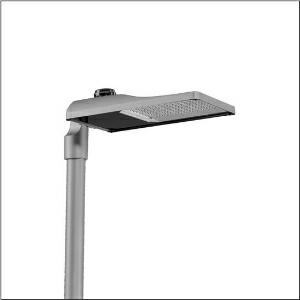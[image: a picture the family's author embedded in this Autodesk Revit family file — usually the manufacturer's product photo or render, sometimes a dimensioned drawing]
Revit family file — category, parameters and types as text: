
# Revit family: streetlight_sl_31_maxi___pl52_5xh8h75n08sa_385d
name_source: partatom
category: Lighting Fixtures
units: mm (PartAtom-declared; Revit-internal decimal feet)

## family parameters
Cut with Voids When Loaded = No
Host = Face
Light Source = No
Part Type = Normal
Room Calculation Point = No
Round Connector Dimension = Use Diameter
Shared = No

## types (1)
- --- (1 x LED, 22010 lm, 208.6 W, 2200K)
    Apparent Load = 209 VA
    CIE Flux Codes = 27 59 98 100 100
    Color Rendering = 70
    Color Temperature = 2200K
    Default Elevation = 1800 mm
    Description = Streetlight SL 31 maxi NEMA (7pin), Desk-Remote mast luminaire for post-top, side-entry; light control with lens of PMMA; light distribution: PL52, direct asymmetric distribution, for standard-compliant lighting for roads and squares; LED: luminous flux: 22.010lm, light colour: 722, colour temperature: 2200K; luminous efficacy: 105,5lm/W; control: pre-setting: linear dimming characteristic, flexible luminous flux parameterisation, time-dependent luminous flux control, constant luminous flux control, intelligent temperature release in ECG and LED module, overheat protection; luminaire housing, of diecast aluminium, Siteco® metallic grey (DB 702S), corrosivity category C5 high according to DIN EN ISO 12944; cover of toughened safety glass, transparent, opened without tools; mast flange of diecast aluminium, Siteco® metallic grey (DB 702S), spigot size: 76/60mm, mast flange included unmounted; with cable H07RN-F 3x 1.5mm², cable length: 14,5m, connection cable pre-assembled; mains connection: 220..240V, AC, 50/60Hz; power consumption (at start of service life): 208,6W / (at end of service life): 233,1W / (with reduced operation 50%): 88W; protection rating (complete): IP66; insulation class (complete): insulation class I (protective earthing); impact resistance: IK10; certification: CE, ENEC, ENEC+, VDE, UKCA; permissible operating ambient temperature for outdoor applications: -40..+50°C; packaging unit: 1 piece

Light Distribution: PL52
    Height = 79 mm
    Lamp = 1 x LED
    Lamp Light Flux = 22010 lm
    Lamp Power = 208.6 W
    Lamp count = 1
    Length = 657 mm
    Luminous efficacy = 106 lm/W
    Manufacturer = Siteco
    ModVariant = No
    Model = 5XH8H75N08SA
    Number of Poles = 1
    OnlyDefault = Yes
    Power Factor = 1
    Product Name = Streetlight SL 31 maxi | PL52
    Product group = mast luminaire | pylon top
    ProductGroupID = 6100
    Protection Class = Protection class I
    Protection Degree = IP 66
    RLX_Detail_Level = 1
    RLX_Emergency_Light_Flux = 0 lm
    RLX_Emergency_Type = 0
    RLX_Emergency_Type_DB = No
    RlxData = <blob elided: 36537 chars, md5=4420bb70>
    Socket = socket
    Standby Power = 0 W
    System Light Flux = 22009 lm
    System Power = 209 W
    Type Comments = factory setting: luminous flux: 100 % | dim-lin: 254 | 718 mA
    Type Image = l_1300293.jpg
    URL = http://relux.com
    VarID = @adj_008215
    Voltage = 0 V
    Weight = 0.00 kg
    Width = 362 mm

## geometry (parser evidence)
native form markers: Blend x4, Sweep x11
no freeform markers — native parametric forms only
